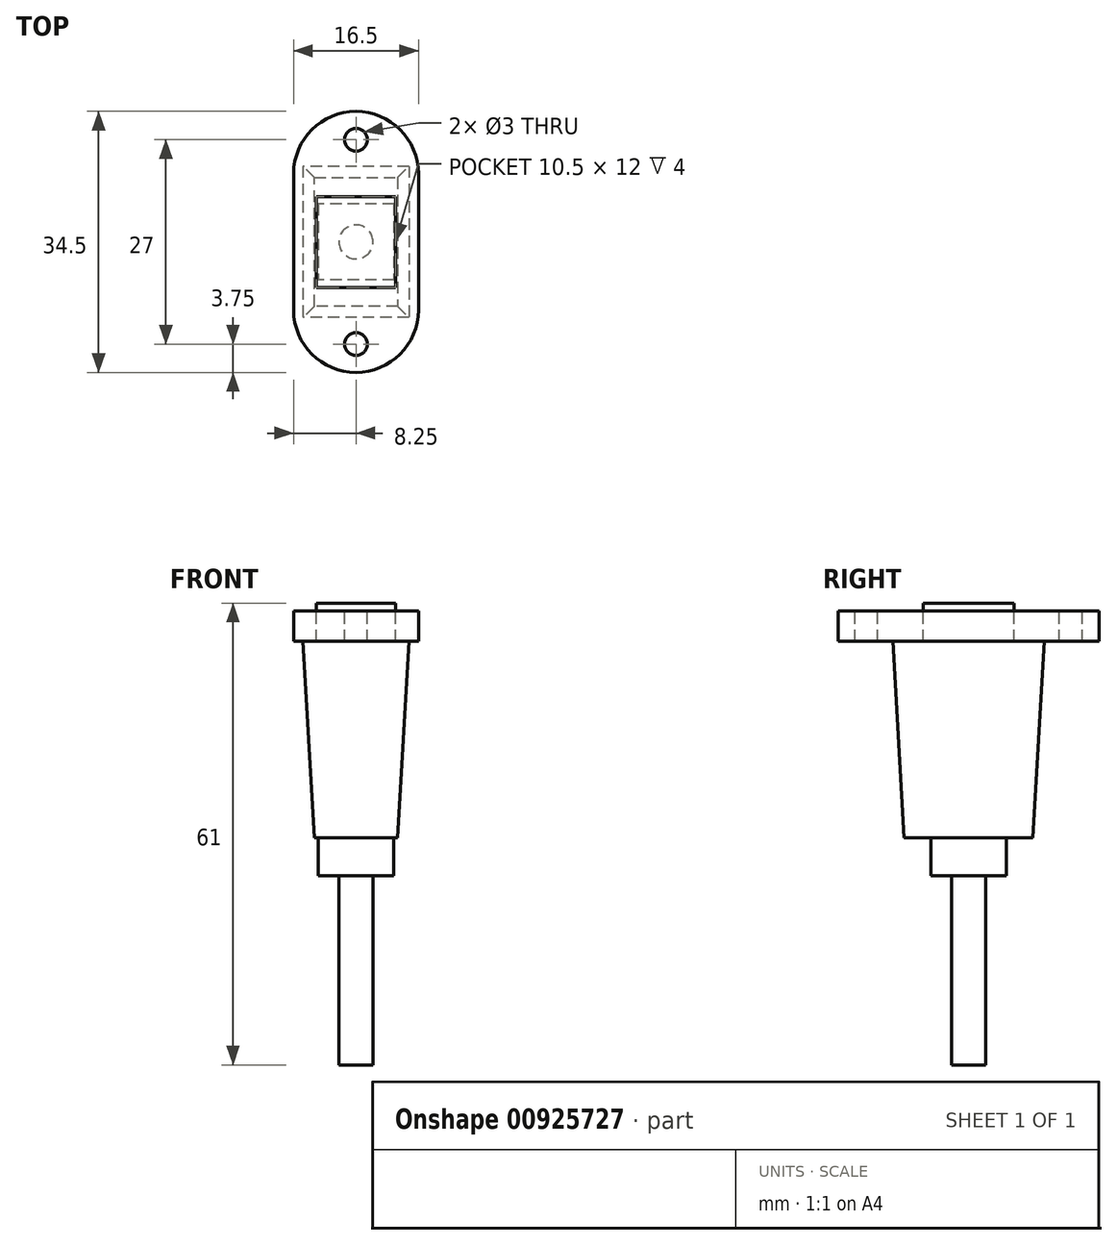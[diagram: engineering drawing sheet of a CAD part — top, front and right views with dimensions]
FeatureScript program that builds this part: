
annotation { "Feature Type Name" : "Feature", "Feature Type Description" : "" }
export const myFeature = defineFeature(function(context is Context, id is Id, definition is map)
    precondition{}
    {
        {
            var Q0;
            Q0=qCreatedBy(makeId("Top.planeOp"),FACE);
            var sketch = newSketch(context, id + "F0", { "sketchPlane" : qUnion([Q0])});
            skLineSegment(sketch, "E0.bottom", {"start": v(5.25, -6) * mm, "end": v(-5.25, -6) * mm});
            skLineSegment(sketch, "E0.top", {"start": v(5.25, 6) * mm, "end": v(-5.25, 6) * mm});
            skLineSegment(sketch, "E0.left", {"start": v(5.25, -6) * mm, "end": v(5.25, 6) * mm});
            skLineSegment(sketch, "E0.right", {"start": v(-5.25, -6) * mm, "end": v(-5.25, 6) * mm});
            skPoint(sketch, "E0.middle", {"position": v(0, 0) * mm});
            skLineSegment(sketch, "E1.bottom", {"start": v(8.25, -9) * mm, "end": v(-8.25, -9) * mm});
            skLineSegment(sketch, "E1.top", {"start": v(8.25, 9) * mm, "end": v(-8.25, 9) * mm});
            skLineSegment(sketch, "E1.left", {"start": v(8.25, -9) * mm, "end": v(8.25, 9) * mm});
            skLineSegment(sketch, "E1.right", {"start": v(-8.25, -9) * mm, "end": v(-8.25, 9) * mm});
            skArc(sketch, "E2", {"start": v(8.25, 9) * mm, "mid": v(0, 17.25) * mm, "end": v(-8.25, 9) * mm});
            skArc(sketch, "E3", {"start": v(8.25, -9) * mm, "mid": v(0, -17.25) * mm, "end": v(-8.25, -9) * mm});
            skCircle(sketch, "E4", {"center": v(0, 13.5) * mm, "radius": 1.5 * mm});
            skCircle(sketch, "E5", {"center": v(0, -13.5) * mm, "radius": 1.5 * mm});
            skSolve(sketch);
        }
        {
            var Q0;
            Q0=makeQuery(id+"F0.imprint","IMPRINT",FACE,{"disambiguationData":[TD([[makeQuery(id+"F0.imprint","IMPRINT",EDGE,{"derivedFrom":sQuery(id+"F0.wireOp",EDGE,"E0.bottom")}),1.0]])]});
            var Q1;
            Q1=makeQuery(id+"F0.imprint","IMPRINT",FACE,{"disambiguationData":[TD([[makeQuery(id+"F0.imprint","IMPRINT",EDGE,{"derivedFrom":sQuery(id+"F0.wireOp",EDGE,"E1.top")}),-1.0]])]});
            var Q2;
            Q2=makeQuery(id+"F0.imprint","IMPRINT",FACE,{"disambiguationData":[TD([[makeQuery(id+"F0.imprint","IMPRINT",EDGE,{"derivedFrom":sQuery(id+"F0.wireOp",EDGE,"E1.bottom")}),1.0]])]});
            extrude(context, id + "F1", {"entities" : qUnion([Q0, Q1, Q2]), "oppositeDirection" : true, "depth" : 4 * mm, "offsetDistance" : 25 * mm});
        }
        {
            var Q0;
            Q0=makeQuery(id+"F1.opExtrude","CAP_FACE",FACE,{"disambiguationData":[OSD([sQuery(id+"F0.wireOp",EDGE,"E0.bottom"),sQuery(id+"F0.wireOp",EDGE,"E0.top"),sQuery(id+"F0.wireOp",EDGE,"E0.left"),sQuery(id+"F0.wireOp",EDGE,"E0.right"),sQuery(id+"F0.wireOp",EDGE,"E1.left"),sQuery(id+"F0.wireOp",EDGE,"E1.right"),sQuery(id+"F0.wireOp",EDGE,"E2"),sQuery(id+"F0.wireOp",EDGE,"E3"),sQuery(id+"F0.wireOp",EDGE,"E4"),sQuery(id+"F0.wireOp",EDGE,"E5")])],"isStart":false});
            var sketch = newSketch(context, id + "F2", { "sketchPlane" : qUnion([Q0])});
            skLineSegment(sketch, "E6.bottom", {"start": v(7, -10) * mm, "end": v(-7, -10) * mm});
            skLineSegment(sketch, "E6.top", {"start": v(7, 10) * mm, "end": v(-7, 10) * mm});
            skLineSegment(sketch, "E6.left", {"start": v(7, -10) * mm, "end": v(7, 10) * mm});
            skLineSegment(sketch, "E6.right", {"start": v(-7, -10) * mm, "end": v(-7, 10) * mm});
            skPoint(sketch, "E6.middle", {"position": v(0, 0) * mm});
            skSolve(sketch);
        }
        {
            var Q0;
            Q0=qSketchRegion(id+"F2",true);
            extrude(context, id + "F3", {"entities" : qUnion([Q0]), "operationType" : NewBodyOperationType.ADD, "depth" : 26 * mm, "offsetDistance" : 25 * mm});
        }
        {
            var Q0;
            Q0=makeQuery(id+"F3.opExtrude","CAP_EDGE",EDGE,{"disambiguationData":[OSD([sQuery(id+"F2.wireOp",EDGE,"E6.top")])],"isStart":false});
            var Q1;
            Q1=makeQuery(id+"F3.opExtrude","CAP_EDGE",EDGE,{"disambiguationData":[OSD([sQuery(id+"F2.wireOp",EDGE,"E6.bottom")])],"isStart":false});
            var Q2;
            Q2=makeQuery(id+"F3.opExtrude","CAP_EDGE",EDGE,{"disambiguationData":[OSD([sQuery(id+"F2.wireOp",EDGE,"E6.left")])],"isStart":false});
            var Q3;
            Q3=makeQuery(id+"F3.opExtrude","CAP_EDGE",EDGE,{"disambiguationData":[OSD([sQuery(id+"F2.wireOp",EDGE,"E6.right")])],"isStart":false});
            chamfer(context, id + "F4", {"entities" : qUnion([Q0, Q1, Q2, Q3]), "chamferType" : ChamferType.TWO_OFFSETS, "width1" : 1.5 * mm, "oppositeDirection" : false, "width2" : 26 * mm, "tangentPropagation" : true});
        }
        {
            var Q0;
            Q0=makeQuery(id+"F3.opExtrude","CAP_FACE",FACE,{"disambiguationData":[OSD([sQuery(id+"F2.wireOp",EDGE,"E6.bottom"),sQuery(id+"F2.wireOp",EDGE,"E6.top"),sQuery(id+"F2.wireOp",EDGE,"E6.left"),sQuery(id+"F2.wireOp",EDGE,"E6.right")])],"isStart":false});
            var sketch = newSketch(context, id + "F5", { "sketchPlane" : qUnion([Q0])});
            skLineSegment(sketch, "E7.bottom", {"start": v(5, -5) * mm, "end": v(-5, -5) * mm});
            skLineSegment(sketch, "E7.top", {"start": v(5, 5) * mm, "end": v(-5, 5) * mm});
            skLineSegment(sketch, "E7.left", {"start": v(5, -5) * mm, "end": v(5, 5) * mm});
            skLineSegment(sketch, "E7.right", {"start": v(-5, -5) * mm, "end": v(-5, 5) * mm});
            skPoint(sketch, "E7.middle", {"position": v(0, 0) * mm});
            skSolve(sketch);
        }
        {
            var Q0;
            Q0=qSketchRegion(id+"F5",true);
            extrude(context, id + "F6", {"entities" : qUnion([Q0]), "operationType" : NewBodyOperationType.ADD, "depth" : 5 * mm, "offsetDistance" : 25 * mm});
        }
        {
            var Q0;
            Q0=makeQuery(id+"F6.opExtrude","CAP_FACE",FACE,{"disambiguationData":[OSD([sQuery(id+"F5.wireOp",EDGE,"E7.bottom"),sQuery(id+"F5.wireOp",EDGE,"E7.top"),sQuery(id+"F5.wireOp",EDGE,"E7.left"),sQuery(id+"F5.wireOp",EDGE,"E7.right")])],"isStart":false});
            var sketch = newSketch(context, id + "F7", { "sketchPlane" : qUnion([Q0])});
            skCircle(sketch, "E8", {"center": v(0, 0) * mm, "radius": 2.25 * mm});
            skSolve(sketch);
        }
        {
            var Q0;
            Q0=qSketchRegion(id+"F7",true);
            extrude(context, id + "F8", {"entities" : qUnion([Q0]), "operationType" : NewBodyOperationType.ADD, "depth" : 25 * mm, "offsetDistance" : 25 * mm});
        }
        {
            var Q0;
            Q0=makeQuery(id+"F0.imprint","IMPRINT",FACE,{"disambiguationData":[TD([[makeQuery(id+"F0.imprint","IMPRINT",EDGE,{"derivedFrom":sQuery(id+"F0.wireOp",EDGE,"E0.bottom")}),1.0]])]});
            var sketch = newSketch(context, id + "F9", { "sketchPlane" : qUnion([Q0])});
            skLineSegment(sketch, "E9.bottom", {"start": v(5.25, 6) * mm, "end": v(-5.25, 6) * mm});
            skLineSegment(sketch, "E9.top", {"start": v(5.25, -6) * mm, "end": v(-5.25, -6) * mm});
            skLineSegment(sketch, "E9.left", {"start": v(5.25, 6) * mm, "end": v(5.25, -6) * mm});
            skLineSegment(sketch, "E9.right", {"start": v(-5.25, 6) * mm, "end": v(-5.25, -6) * mm});
            skPoint(sketch, "E9.middle", {"position": v(0, 0) * mm});
            skSolve(sketch);
        }
        {
            var Q0;
            Q0=qSketchRegion(id+"F9",true);
            extrude(context, id + "F10", {"entities" : qUnion([Q0]), "operationType" : NewBodyOperationType.ADD, "depth" : 1 * mm, "offsetDistance" : 25 * mm});
        }
    });
